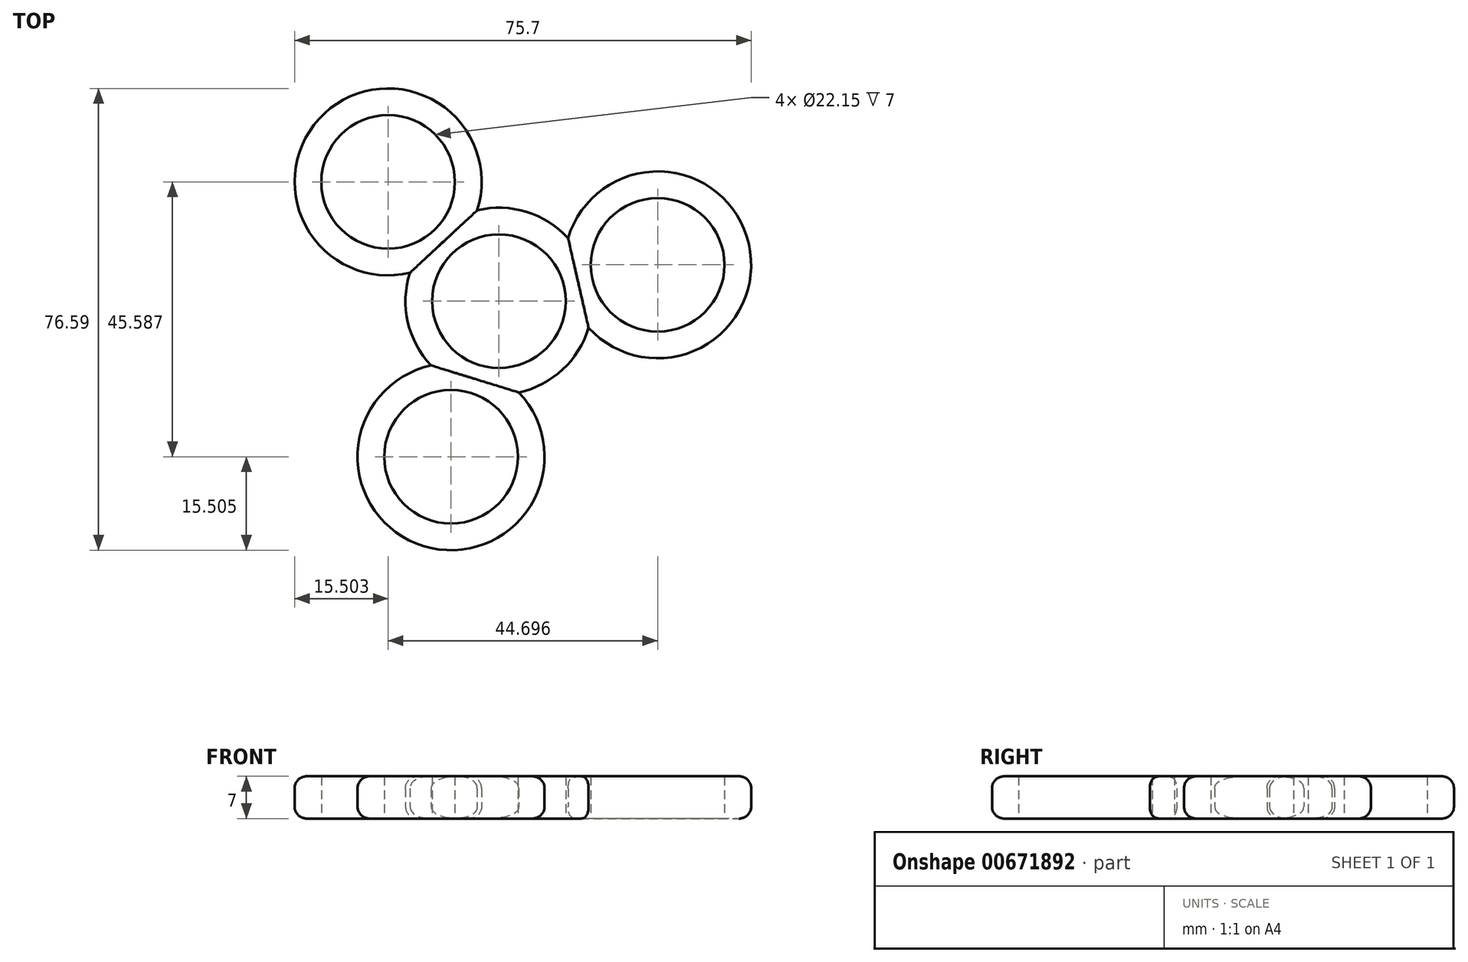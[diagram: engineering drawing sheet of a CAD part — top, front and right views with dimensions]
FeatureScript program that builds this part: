
annotation { "Feature Type Name" : "Feature", "Feature Type Description" : "" }
export const myFeature = defineFeature(function(context is Context, id is Id, definition is map)
    precondition{}
    {
        {
            var Q0;
            Q0=qCreatedBy(makeId("Top.planeOp"),FACE);
            var sketch = newSketch(context, id + "F0", { "sketchPlane" : qUnion([Q0])});
            skCircle(sketch, "E0", {"center": v(0, 0) * mm, "radius": 11.07 * mm});
            skPoint(sketch, "E1", {"position": v(26.32, 6.02) * mm});
            skLineSegment(sketch, "E2", {"start": v(0, 0) * mm, "end": v(26.32, 6.02) * mm});
            skLineSegment(sketch, "E3", {"start": v(0, 0) * mm, "end": v(-7.94, -25.8) * mm});
            skLineSegment(sketch, "E4", {"start": v(0, 0) * mm, "end": v(-18.38, 19.78) * mm});
            skCircle(sketch, "E5", {"center": v(26.32, 6.02) * mm, "radius": 11.07 * mm});
            skCircle(sketch, "E6", {"center": v(-18.38, 19.78) * mm, "radius": 11.07 * mm});
            skCircle(sketch, "E7", {"center": v(-7.94, -25.8) * mm, "radius": 11.07 * mm});
            skCircle(sketch, "E8", {"center": v(0, 0) * mm, "radius": 15.5 * mm});
            skCircle(sketch, "E9", {"center": v(-7.94, -25.8) * mm, "radius": 15.5 * mm});
            skCircle(sketch, "E10", {"center": v(26.32, 6.02) * mm, "radius": 15.5 * mm});
            skCircle(sketch, "E11", {"center": v(-18.38, 19.78) * mm, "radius": 15.5 * mm});
            skSolve(sketch);
        }
        {
            var Q0;
            Q0=makeQuery(id+"F0.imprint","IMPRINT",FACE,{"disambiguationData":[TD([[makeQuery(id+"F0.imprint","IMPRINT",EDGE,{"derivedFrom":sQuery(id+"F0.wireOp",EDGE,"E6")}),-1.0]])]});
            var Q1;
            {var subQ0=sQuery(id+"F0.wireOp",EDGE,"E8");var subQ1=sQuery(id+"F0.wireOp",EDGE,"E4");var subQ2=makeQuery(id+"F0.imprint","INTERSECT",VERTEX,{"derivedFrom":[subQ1,subQ0]});Q1=makeQuery(id+"F0.imprint","IMPRINT",FACE,{"disambiguationData":[TD([[makeQuery(id+"F0.imprint","IMPRINT",EDGE,{"disambiguationData":[TD([[subQ2,1.0]])],"derivedFrom":subQ1}),1.0]])]});}
            var Q2;
            {var subQ0=sQuery(id+"F0.wireOp",EDGE,"E8");var subQ1=sQuery(id+"F0.wireOp",EDGE,"E4");var subQ2=makeQuery(id+"F0.imprint","INTERSECT",VERTEX,{"derivedFrom":[subQ1,subQ0]});Q2=makeQuery(id+"F0.imprint","IMPRINT",FACE,{"disambiguationData":[TD([[makeQuery(id+"F0.imprint","IMPRINT",EDGE,{"disambiguationData":[TD([[subQ2,1.0]])],"derivedFrom":subQ1}),-1.0]])]});}
            var Q3;
            {var subQ7=sQuery(id+"F0.wireOp",EDGE,"E0");var subQ9=sQuery(id+"F0.wireOp",EDGE,"E4");var subQ10=makeQuery(id+"F0.imprint","INTERSECT",VERTEX,{"derivedFrom":[subQ7,subQ9]});Q3=makeQuery(id+"F0.imprint","IMPRINT",FACE,{"disambiguationData":[TD([[makeQuery(id+"F0.imprint","IMPRINT",EDGE,{"disambiguationData":[TD([[subQ10,1.0]])],"derivedFrom":subQ7}),-1.0]])]});}
            var Q4;
            {var subQ0=sQuery(id+"F0.wireOp",EDGE,"E8");var subQ1=sQuery(id+"F0.wireOp",EDGE,"E2");var subQ2=makeQuery(id+"F0.imprint","INTERSECT",VERTEX,{"derivedFrom":[subQ1,subQ0]});Q4=makeQuery(id+"F0.imprint","IMPRINT",FACE,{"disambiguationData":[TD([[makeQuery(id+"F0.imprint","IMPRINT",EDGE,{"disambiguationData":[TD([[subQ2,1.0]])],"derivedFrom":subQ1}),1.0]])]});}
            var Q5;
            {var subQ0=sQuery(id+"F0.wireOp",EDGE,"E8");var subQ1=sQuery(id+"F0.wireOp",EDGE,"E2");var subQ2=makeQuery(id+"F0.imprint","INTERSECT",VERTEX,{"derivedFrom":[subQ1,subQ0]});Q5=makeQuery(id+"F0.imprint","IMPRINT",FACE,{"disambiguationData":[TD([[makeQuery(id+"F0.imprint","IMPRINT",EDGE,{"disambiguationData":[TD([[subQ2,1.0]])],"derivedFrom":subQ1}),-1.0]])]});}
            var Q6;
            {var subQ0=sQuery(id+"F0.wireOp",EDGE,"E2");var subQ1=sQuery(id+"F0.wireOp",EDGE,"E0");var subQ2=makeQuery(id+"F0.imprint","INTERSECT",VERTEX,{"derivedFrom":[subQ1,subQ0]});Q6=makeQuery(id+"F0.imprint","IMPRINT",FACE,{"disambiguationData":[TD([[makeQuery(id+"F0.imprint","IMPRINT",EDGE,{"disambiguationData":[TD([[subQ2,1.0]])],"derivedFrom":subQ1}),-1.0]])]});}
            var Q7;
            {var subQ0=sQuery(id+"F0.wireOp",EDGE,"E8");var subQ1=sQuery(id+"F0.wireOp",EDGE,"E3");var subQ2=makeQuery(id+"F0.imprint","INTERSECT",VERTEX,{"derivedFrom":[subQ1,subQ0]});Q7=makeQuery(id+"F0.imprint","IMPRINT",FACE,{"disambiguationData":[TD([[makeQuery(id+"F0.imprint","IMPRINT",EDGE,{"disambiguationData":[TD([[subQ2,1.0]])],"derivedFrom":subQ1}),1.0]])]});}
            var Q8;
            {var subQ0=sQuery(id+"F0.wireOp",EDGE,"E8");var subQ1=sQuery(id+"F0.wireOp",EDGE,"E3");var subQ2=makeQuery(id+"F0.imprint","INTERSECT",VERTEX,{"derivedFrom":[subQ1,subQ0]});Q8=makeQuery(id+"F0.imprint","IMPRINT",FACE,{"disambiguationData":[TD([[makeQuery(id+"F0.imprint","IMPRINT",EDGE,{"disambiguationData":[TD([[subQ2,1.0]])],"derivedFrom":subQ1}),-1.0]])]});}
            var Q9;
            {var subQ5=sQuery(id+"F0.wireOp",EDGE,"E4");var subQ7=sQuery(id+"F0.wireOp",EDGE,"E0");var subQ8=makeQuery(id+"F0.imprint","INTERSECT",VERTEX,{"derivedFrom":[subQ7,subQ5]});Q9=makeQuery(id+"F0.imprint","IMPRINT",FACE,{"disambiguationData":[TD([[makeQuery(id+"F0.imprint","IMPRINT",EDGE,{"disambiguationData":[TD([[subQ8,-1.0]])],"derivedFrom":subQ7}),-1.0]])]});}
            var Q10;
            Q10=makeQuery(id+"F0.imprint","IMPRINT",FACE,{"disambiguationData":[TD([[makeQuery(id+"F0.imprint","IMPRINT",EDGE,{"derivedFrom":sQuery(id+"F0.wireOp",EDGE,"E7")}),-1.0]])]});
            var Q11;
            Q11=makeQuery(id+"F0.imprint","IMPRINT",FACE,{"disambiguationData":[TD([[makeQuery(id+"F0.imprint","IMPRINT",EDGE,{"derivedFrom":sQuery(id+"F0.wireOp",EDGE,"E5")}),-1.0]])]});
            extrude(context, id + "F1", {"entities" : qUnion([Q0, Q1, Q2, Q3, Q4, Q5, Q6, Q7, Q8, Q9, Q10, Q11]), "depth" : 7 * mm, "offsetDistance" : 25 * mm});
        }
        {
            var Q0;
            Q0=makeQuery(id+"F1.opExtrude","CAP_EDGE",EDGE,{"disambiguationData":[OSD([sQuery(id+"F0.wireOp",EDGE,"E10")])],"isStart":true});
            var Q1;
            {var subQ0=sQuery(id+"F0.wireOp",EDGE,"E8");Q1=makeQuery(id+"F1.opExtrude","CAP_EDGE",EDGE,{"disambiguationData":[OSD([subQ0]),TDD([makeQuery(id+"F0.imprint","IMPRINT",EDGE,{"disambiguationData":[TD([[makeQuery(id+"F0.imprint","INTERSECT",VERTEX,{"disambiguationData":[OD(1.0)],"derivedFrom":[subQ0,sQuery(id+"F0.wireOp",EDGE,"E9")]}),-1.0]])],"derivedFrom":subQ0})])],"isStart":true});}
            var Q2;
            Q2=makeQuery(id+"F1.opExtrude","CAP_EDGE",EDGE,{"disambiguationData":[OSD([sQuery(id+"F0.wireOp",EDGE,"E9")])],"isStart":true});
            var Q3;
            {var subQ0=sQuery(id+"F0.wireOp",EDGE,"E8");Q3=makeQuery(id+"F1.opExtrude","CAP_EDGE",EDGE,{"disambiguationData":[OSD([subQ0]),TDD([makeQuery(id+"F0.imprint","IMPRINT",EDGE,{"disambiguationData":[TD([[makeQuery(id+"F0.imprint","INTERSECT",VERTEX,{"disambiguationData":[OD(1.0)],"derivedFrom":[subQ0,sQuery(id+"F0.wireOp",EDGE,"E11")]}),-1.0]])],"derivedFrom":subQ0})])],"isStart":true});}
            var Q4;
            Q4=makeQuery(id+"F1.opExtrude","CAP_EDGE",EDGE,{"disambiguationData":[OSD([sQuery(id+"F0.wireOp",EDGE,"E11")])],"isStart":true});
            var Q5;
            {var subQ0=sQuery(id+"F0.wireOp",EDGE,"E8");Q5=makeQuery(id+"F1.opExtrude","CAP_EDGE",EDGE,{"disambiguationData":[OSD([subQ0]),TDD([makeQuery(id+"F0.imprint","IMPRINT",EDGE,{"disambiguationData":[TD([[makeQuery(id+"F0.imprint","INTERSECT",VERTEX,{"disambiguationData":[OD(0.0)],"derivedFrom":[subQ0,sQuery(id+"F0.wireOp",EDGE,"E10")]}),-1.0]])],"derivedFrom":subQ0})])],"isStart":true});}
            fillet(context, id + "F2", {"entities" : qUnion([Q0, Q1, Q2, Q3, Q4, Q5]), "radius" : 2 * mm, "tangentPropagation" : true, "allowEdgeOverflow" : false});
        }
        {
            var Q0;
            Q0=makeQuery(id+"F1.opExtrude","CAP_EDGE",EDGE,{"disambiguationData":[OSD([sQuery(id+"F0.wireOp",EDGE,"E9")])],"isStart":false});
            var Q1;
            {var subQ0=sQuery(id+"F0.wireOp",EDGE,"E8");Q1=makeQuery(id+"F1.opExtrude","CAP_EDGE",EDGE,{"disambiguationData":[OSD([subQ0]),TDD([makeQuery(id+"F0.imprint","IMPRINT",EDGE,{"disambiguationData":[TD([[makeQuery(id+"F0.imprint","INTERSECT",VERTEX,{"disambiguationData":[OD(1.0)],"derivedFrom":[subQ0,sQuery(id+"F0.wireOp",EDGE,"E9")]}),-1.0]])],"derivedFrom":subQ0})])],"isStart":false});}
            var Q2;
            Q2=makeQuery(id+"F1.opExtrude","CAP_EDGE",EDGE,{"disambiguationData":[OSD([sQuery(id+"F0.wireOp",EDGE,"E10")])],"isStart":false});
            var Q3;
            {var subQ0=sQuery(id+"F0.wireOp",EDGE,"E8");Q3=makeQuery(id+"F1.opExtrude","CAP_EDGE",EDGE,{"disambiguationData":[OSD([subQ0]),TDD([makeQuery(id+"F0.imprint","IMPRINT",EDGE,{"disambiguationData":[TD([[makeQuery(id+"F0.imprint","INTERSECT",VERTEX,{"disambiguationData":[OD(0.0)],"derivedFrom":[subQ0,sQuery(id+"F0.wireOp",EDGE,"E10")]}),-1.0]])],"derivedFrom":subQ0})])],"isStart":false});}
            var Q4;
            {var subQ0=sQuery(id+"F0.wireOp",EDGE,"E8");Q4=makeQuery(id+"F1.opExtrude","CAP_EDGE",EDGE,{"disambiguationData":[OSD([subQ0]),TDD([makeQuery(id+"F0.imprint","IMPRINT",EDGE,{"disambiguationData":[TD([[makeQuery(id+"F0.imprint","INTERSECT",VERTEX,{"disambiguationData":[OD(1.0)],"derivedFrom":[subQ0,sQuery(id+"F0.wireOp",EDGE,"E11")]}),-1.0]])],"derivedFrom":subQ0})])],"isStart":false});}
            var Q5;
            Q5=makeQuery(id+"F1.opExtrude","CAP_EDGE",EDGE,{"disambiguationData":[OSD([sQuery(id+"F0.wireOp",EDGE,"E11")])],"isStart":false});
            fillet(context, id + "F3", {"entities" : qUnion([Q0, Q1, Q2, Q3, Q4, Q5]), "radius" : 2 * mm, "tangentPropagation" : true, "allowEdgeOverflow" : false});
        }
    });
